# Revit family: Haworth_Planes_ColumnBaseConferenceTable_PebbleOnePiece
name_source: partatom
category: Furniture Systems
revit_build: Autodesk Revit 2018 (Build: 20170223_1515(x64)
units: mm (PartAtom-declared; Revit-internal decimal feet)

## family parameters
Always vertical = Yes
Cut with Voids When Loaded = No
OmniClass Number = 23.40.70.14.64.21
OmniClass Title = Systems Furniture
Part Type = Normal
Room Calculation Point = No
Round Connector Dimension = Use Diameter
Shared = No
Work Plane-Based = No

## types (1)
- 120w 60d
    Actual Depth = 60"
    Actual Height = 41"
    Actual Width = 120"
    Assembly Code = E2020200
    Base Finish = Haworth _ Metal _ Brushed Aluminum
    Custom Size = No
    Cutout Depth = 4"
    Cutout Width = 8"
    Depth = 60"
    Description = Haworth - Planes - Column Base Conference Table - Pebble - One-Piece
    Flip Top = Yes
    Flip Top Finish = Haworth _ Paint _ Metallic Champagne
    Fliptop Center Control = Yes
    Fliptop Depth = 4 3/8"
    Fliptop Side Control = No
    Fliptop Side Offset = 30"
    Fliptop Width = 8 1/4"
    Height = 41"
    Manufacturer = Haworth
    Max. Depth = 60"
    Max. Height = 41"
    Max. Width = 120"
    Min. Depth = 42"
    Min. Height = 21"
    Min. Width = 96"
    Model = TARP
    Opening Center = Yes
    Opening Double = No
    Opening Double Wide = No
    Opening Left/Right = No
    Opening Single = Yes
    Opening Single Wide = No
    Revision Number = 1
    Size = Verify Final Dim. w/ Haworth
    Standard Depths = 42, 48, 54, 60 in.
    Standard Heights = 21, 29, 41 in.
    Standard Widths = 96, 102, 108, 114, 120 in.
    Support Height = 39 13/16"
    Support Side Offset = 30"
    Sustainability Info = https://haworth.com
    Table Thickness = 1 3/16"
    Trim Finish = Haworth _ Laminate _ Maple H-AE
    URL = www.haworth.com
    URL - Product = https://www.haworth.com
    Warranty = https://www.haworth.com
    Width = 120"

## geometry (parser evidence)
native form markers: Sweep x10
no freeform markers — native parametric forms only
